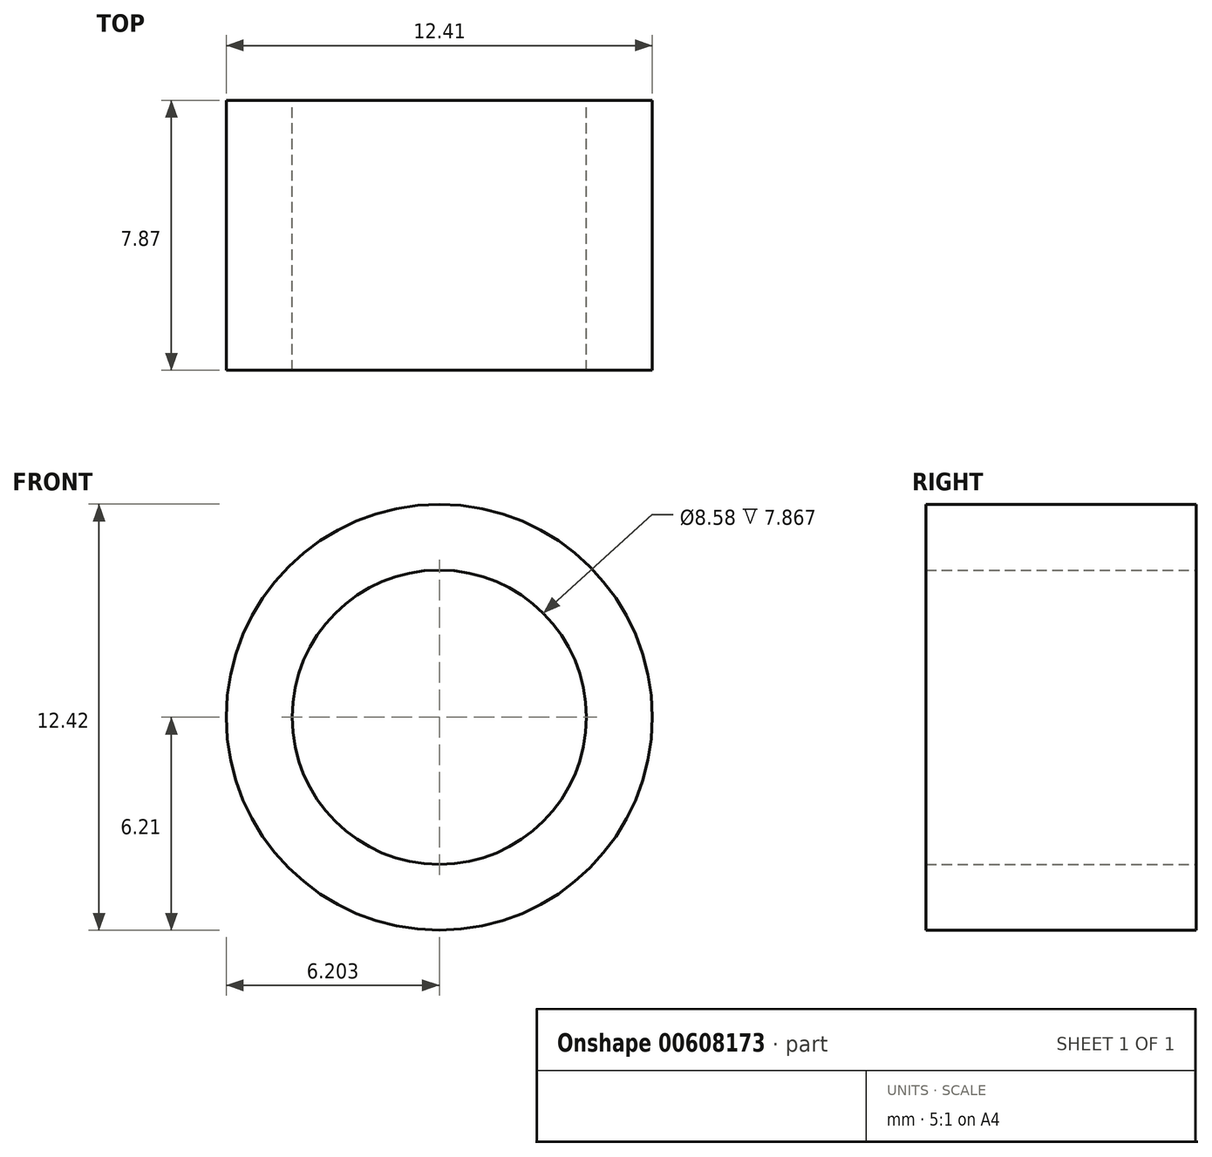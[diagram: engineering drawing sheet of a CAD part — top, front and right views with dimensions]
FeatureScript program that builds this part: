
annotation { "Feature Type Name" : "Feature", "Feature Type Description" : "" }
export const myFeature = defineFeature(function(context is Context, id is Id, definition is map)
    precondition{}
    {
        {
            var Q0;
            Q0=qCreatedBy(makeId("Front.planeOp"),FACE);
            var sketch = newSketch(context, id + "F0", { "sketchPlane" : qUnion([Q0])});
            skCircle(sketch, "E0", {"center": v(66.08, 0) * mm, "radius": 4.29 * mm});
            skCircle(sketch, "E1", {"center": v(66.08, 0) * mm, "radius": 6.2 * mm});
            skSolve(sketch);
        }
        {
            var Q0;
            Q0 = qSketchRegion(id + "F0", true);
            extrude(context, id + "F1", {"entities" : qUnion([Q0]), "depth" : 7.87 * mm, "offsetDistance" : 25.4 * mm});
        }
    });
